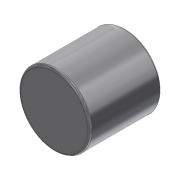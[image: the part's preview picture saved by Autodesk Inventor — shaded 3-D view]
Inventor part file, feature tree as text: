
AUTODESK INVENTOR PART (.ipt)
format: ipt  version: 2014 (Build 180170000, 170)  size: 93,184 bytes
history: native  units: mm
features: extrude x1, fillet x1, sketch x1
ambient origin geometry x8: Origin, YZ Plane, XZ Plane, XY Plane, X Axis, Y Axis, Z Axis, Center Point
bodies: Solid1 (feature_tree)
feature tree (3):
  extrude  "Extrusion1"  Depth=10.0mm TaperAngle=0.0deg
  fillet  "Fillet1"  Radius=0.3mm
  sketch  "Sketch1"  dims[d0=10.0mm d1=10.0mm d2=0.0mm d3=0.3mm]
